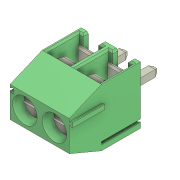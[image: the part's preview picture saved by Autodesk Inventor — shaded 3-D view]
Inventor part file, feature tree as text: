
AUTODESK INVENTOR PART (.ipt)
format: ipt  version: 2022 (Build 260153000, 153)  size: 323,072 bytes
history: imported  units: in
note: dims shown in document units (in); Inventor stores cm internally (conversion verified against a paired STEP export)
features: sketch x2, imported_body x1
ambient origin geometry x8: Origin, YZ Plane, XZ Plane, XY Plane, X Axis, Y Axis, Z Axis, Center Point
bodies: Solid1 (imported_parasolid), Solid2 (imported_parasolid), Solid3 (imported_parasolid), Solid4 (imported_parasolid), Solid5 (imported_parasolid), Body1 (imported_parasolid), Body2 (imported_parasolid), Body3 (imported_parasolid), Body4 (imported_parasolid), Body5 (imported_parasolid)
feature tree (3):
  sketch  "Sketch1"
  sketch  "Sketch2"
  imported_body  NMx_Import_Brep_tag  [imported B-rep: ~29 faces, bbox_mm=[4.85, 3.8, 5.39]]
